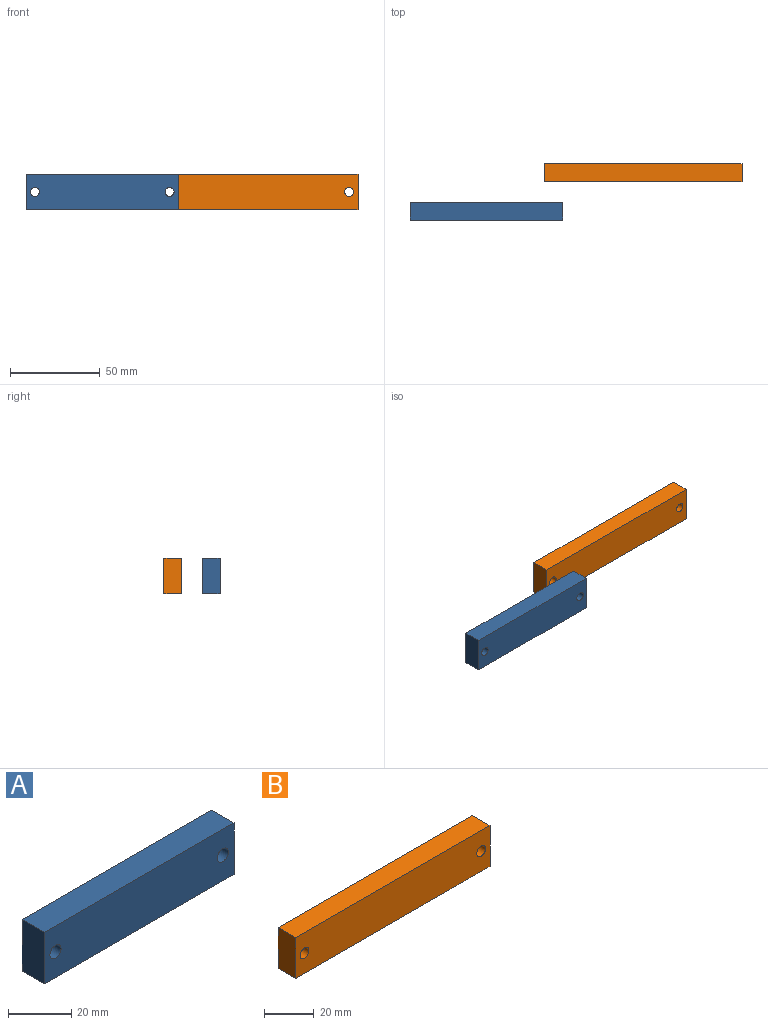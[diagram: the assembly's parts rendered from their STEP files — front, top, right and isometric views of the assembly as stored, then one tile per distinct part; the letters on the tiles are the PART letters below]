
ASSEMBLY  parts=2 mates=1
PART A: 8 faces, bbox 85x10x20 mm
  f0: plane 20x10mm, normal (-1,0,0), area 200mm2, adj f1,f3,f4,f5
  f1: plane 85x10mm, normal (0,0,-1), area 850mm2, adj f0,f2,f4,f5
  f2: plane 20x10mm, normal (1,0,0), area 200mm2, adj f1,f3,f4,f5
  f3: plane 85x10mm, normal (0,0,1), area 850mm2, adj f0,f2,f4,f5
  f4: plane 85x20mm, normal (0,-1,0), area 1660.7mm2, adj f0,f1,f2,f3,f6,f7
  f5: plane 85x20mm, normal (0,1,0), area 1660.7mm2, adj f0,f1,f2,f3,f6,f7
  f6: cylinder r=2.5mm len=10mm, axis (0,-1,0), area 157.1mm2, adj f4,f5
  f7: cylinder r=2.5mm len=10mm, axis (0,-1,0), area 157.1mm2, adj f4,f5
PART B: 8 faces, bbox 110x10x20 mm
  f0: plane 20x10mm, normal (-1,0,0), area 200mm2, adj f1,f3,f4,f5
  f1: plane 110x10mm, normal (0,0,-1), area 1100mm2, adj f0,f2,f4,f5
  f2: plane 20x10mm, normal (1,0,0), area 200mm2, adj f1,f3,f4,f5
  f3: plane 110x10mm, normal (0,0,1), area 1100mm2, adj f0,f2,f4,f5
  f4: plane 110x20mm, normal (0,-1,0), area 2160.7mm2, adj f0,f1,f2,f3,f6,f7
  f5: plane 110x20mm, normal (0,1,0), area 2160.7mm2, adj f0,f1,f2,f3,f6,f7
  f6: cylinder r=2.5mm len=10mm, axis (0,-1,0), area 157.1mm2, adj f4,f5
  f7: cylinder r=2.5mm len=10mm, axis (0,-1,0), area 157.1mm2, adj f4,f5
PLACE A t=(-9.43,18.26,13.32)mm
PLACE B t=(65.57,39.64,13.32)mm
MATE cylindrical B.f7 <-> A.f6  axis (0,-1,0) through (70.57,29.64,23.32)mm
